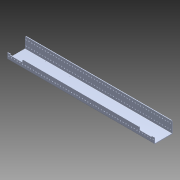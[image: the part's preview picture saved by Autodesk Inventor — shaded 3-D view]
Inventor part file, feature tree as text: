
AUTODESK INVENTOR PART (.ipt)
format: ipt  version: 2015 SP1 (Build 190203100, 203)  size: 510,464 bytes
history: native  units: in
note: dims shown in document units (in); Inventor stores cm internally (conversion verified against a paired STEP export)
features: projected_geometry x8, extrude x3, sketch x3, other x2, chamfer x2, imported_body x1
ambient origin geometry x8: Origin, YZ Plane, XZ Plane, XY Plane, X Axis, Y Axis, Z Axis, Center Point
bodies: Body1 (feature_tree)
feature tree (19):
  other  "LPattern4"
  other  "AM14U2 End Sheet1"
  extrude  "Extrusion1"  Depth=0.125in TaperAngle=45.0deg
  chamfer  "Chamfer1"  Distance=0.75in
  extrude  "Extrusion2"  Depth=2.25in
  chamfer  "Chamfer2"  Distance=0.75in
  extrude  "Extrusion3"  Depth=0.5in
  imported_body  "Base1"
  sketch  "Sketch1"  dims[d0=4.0in d1=0.0in d2=0.125in d3=0.125in d4=45.0deg]
  projected_geometry  "Projected Loop1"
  projected_geometry  "Projected Loop2"
  projected_geometry  "Projected Loop3"
  projected_geometry  "Projected Loop4"
  projected_geometry  "Projected Loop5"
  projected_geometry  "Projected Loop6"
  projected_geometry  "Projected Loop7"
  sketch  "Sketch2"  dims[d5=2.25in]
  projected_geometry  "Projected Loop8"
  sketch  "Sketch3"  dims[d6=0.5in d7=0.75in d8=2.25in d9=0.75in d10=0.5in d11=1.0in d12=0.0in d13=0.125in d14=0.125in d15=45.0deg d16=1.0in d17=0.0in]
